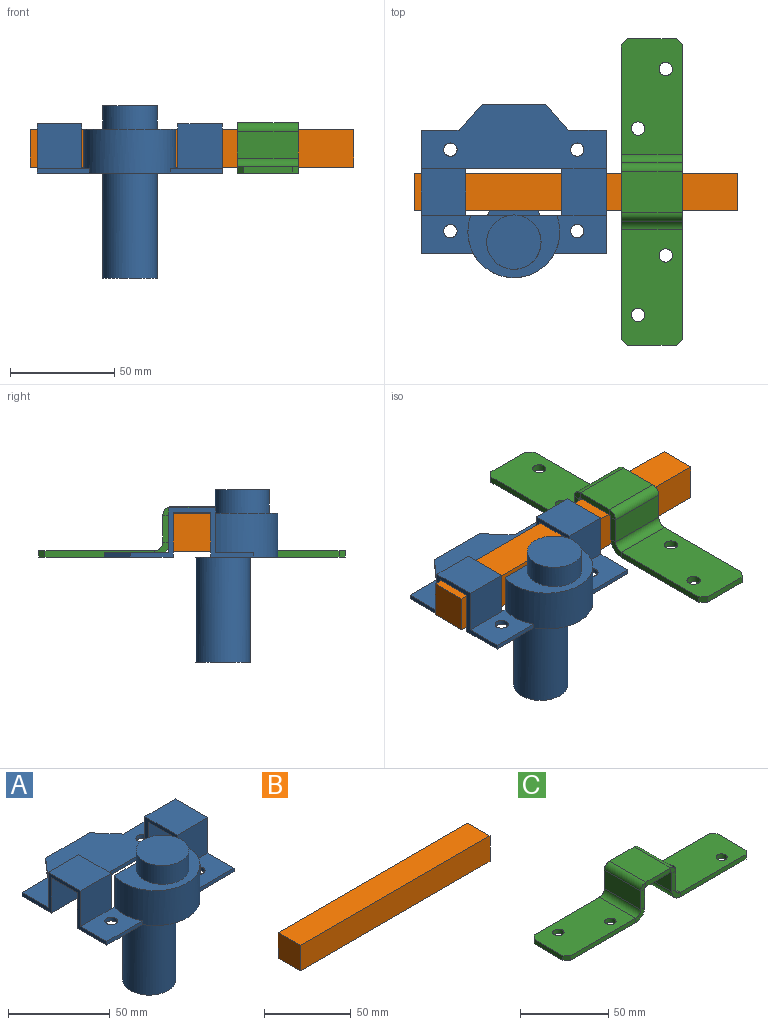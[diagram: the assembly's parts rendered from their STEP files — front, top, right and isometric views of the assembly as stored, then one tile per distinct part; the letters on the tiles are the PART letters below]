
ASSEMBLY  parts=3 mates=1
PART A: 42 faces, bbox 88.5x83x82.7 mm
  f0: plane 88.5x31.95mm, normal (0,0,-1), area 1605.4mm2, adj f1,f2,f3,f4,f13,f14,f15,f22
  f1: plane 59x23.5mm, normal (-1,0,0), area 223.5mm2, adj f0,f5,f6,f7,f8,f9,f10,f12
  f2: plane 59x23.5mm, normal (1,0,0), area 223.5mm2, adj f0,f7,f9,f15,f16,f19,f29,f30
  f3: plane 23.5x22.5mm, normal (-1,0,0), area 143.2mm2, adj f0,f7,f29,f30,f31,f33,f35,f39
  f4: plane 23.5x22.5mm, normal (1,0,0), area 143.2mm2, adj f0,f5,f6,f7,f8,f33,f35,f36
  f5: plane 21.3x21.25mm, normal (0,-1,0), area 452.6mm2, adj f1,f4,f8,f10
  f6: plane 21.3x21.25mm, normal (0,1,0), area 452.6mm2, adj f1,f4,f8,f9
  f7: plane 88.5x32.98mm, normal (0,0,-1), area 2164.3mm2, adj f1,f2,f3,f4,f11,f12,f16,f17
  f8: plane 22.5x21.25mm, normal (0,0,1), area 478.1mm2, adj f1,f4,f5,f6
  f9: plane 88.5x30.78mm, normal (0,0,1), area 2070.8mm2, adj f1,f2,f6,f11,f12,f16,f17,f18
  f10: plane 24.92x18.25mm, normal (0,0,1), area 386.6mm2, adj f1,f5,f13,f14,f23,f33
  f11: plane 12.53x11mm, normal (-0.75,0.66,0), area 36.7mm2, adj f7,f9,f12,f18
  f12: plane 18x2.2mm, normal (0,1,0), area 39.6mm2, adj f1,f7,f9,f11
  f13: plane 24.92x2.2mm, normal (0,-1,0), area 54.8mm2, adj f0,f1,f10,f14
  f14: cylinder r=22mm len=44mm, axis (0,0,-1), area 1701mm2, adj f0,f10,f13,f15,f19,f24,f33
  f15: plane 24.92x2.2mm, normal (0,-1,0), area 54.8mm2, adj f0,f2,f14,f19
  f16: plane 18x2.2mm, normal (0,1,0), area 39.6mm2, adj f2,f7,f9,f17
  f17: plane 12.53x11mm, normal (0.75,0.66,0), area 36.7mm2, adj f7,f9,f16,f18
  f18: plane 30.5x2.2mm, normal (0,1,0), area 67.1mm2, adj f7,f9,f11,f17
  f19: plane 24.92x18.25mm, normal (0,0,1), area 386.6mm2, adj f2,f14,f15,f22,f31,f33
  f20: cylinder r=3.2mm len=6.4mm, axis (0,0,-1), area 44.2mm2, adj f7,f9
  f21: cylinder r=3.2mm len=6.4mm, axis (0,0,-1), area 44.2mm2, adj f7,f9
  f22: cylinder r=3.2mm len=6.4mm, axis (0,0,-1), area 44.2mm2, adj f0,f19
  f23: cylinder r=3.2mm len=6.4mm, axis (0,0,-1), area 44.2mm2, adj f0,f10
  f24: plane 44x29.75mm, normal (0,0,1), area 564mm2, adj f14,f25,f33
  f25: cylinder r=13mm len=26mm, axis (0,0,-1), area 906.1mm2, adj f24,f26,f32,f33
  f26: plane 26x26mm, normal (0,0,1), area 530.9mm2, adj f25
  f27: cylinder r=13mm len=50.4mm, axis (0,0,1), area 4116.7mm2, adj f0,f28,f34
  f28: plane 26x26mm, normal (0,0,-1), area 530.9mm2, adj f27
  f29: plane 21.3x21.25mm, normal (0,1,0), area 452.6mm2, adj f2,f3,f9,f30
  f30: plane 22.5x21.25mm, normal (0,0,1), area 478.1mm2, adj f2,f3,f29,f31
  f31: plane 21.3x21.25mm, normal (0,-1,0), area 452.6mm2, adj f2,f3,f19,f30
  f32: plane 5.07x0.25mm, normal (0,0,-1), area 0.8mm2, adj f25,f33
  f33: plane 46x23.5mm, normal (0,1,0), area 888.1mm2, adj f0,f3,f4,f10,f14,f19,f24,f25
  f34: plane 25.04x9.5mm, normal (0,0,1), area 175.6mm2, adj f27,f33
  f35: plane 46x2.2mm, normal (0,-1,0), area 101.2mm2, adj f3,f4,f7,f9
  f36: plane 21.3x21.25mm, normal (0,1,0), area 452.6mm2, adj f0,f1,f4,f37
  f37: plane 21.25x18.1mm, normal (0,0,-1), area 384.6mm2, adj f1,f4,f36,f38
  f38: plane 21.3x21.25mm, normal (0,-1,0), area 452.6mm2, adj f1,f4,f7,f37
  f39: plane 21.3x21.25mm, normal (0,-1,0), area 452.6mm2, adj f2,f3,f7,f40
  f40: plane 21.25x18.1mm, normal (0,0,-1), area 384.6mm2, adj f2,f3,f39,f41
  f41: plane 21.3x21.25mm, normal (0,1,0), area 452.6mm2, adj f0,f2,f3,f40
PART B: 6 faces, bbox 155x18x18 mm
  f0: plane 155x18mm, normal (0,1,0), area 2790mm2, adj f1,f3,f4,f5
  f1: plane 155x18mm, normal (0,0,-1), area 2790mm2, adj f0,f2,f4,f5
  f2: plane 155x18mm, normal (0,-1,0), area 2790mm2, adj f1,f3,f4,f5
  f3: plane 155x18mm, normal (0,0,1), area 2790mm2, adj f0,f2,f4,f5
  f4: plane 18x18mm, normal (1,0,0), area 324mm2, adj f0,f1,f2,f3
  f5: plane 18x18mm, normal (-1,0,0), area 324mm2, adj f0,f1,f2,f3
PART C: 46 faces, bbox 146.8x29.2x24.1 mm
  f0: plane 12.9x3.1mm, normal (0,1,0), area 40mm2, adj f2,f3,f30,f43
  f1: plane 12.9x3.1mm, normal (0,-1,0), area 40mm2, adj f2,f3,f29,f42
  f2: plane 29.2x12.9mm, normal (1,0,0), area 376.7mm2, adj f0,f1,f32,f44
  f3: plane 29.2x12.9mm, normal (-1,0,0), area 376.7mm2, adj f0,f1,f31,f45
  f4: plane 19.75x3.1mm, normal (0,1,0), area 61.2mm2, adj f6,f7,f26,f30
  f5: plane 19.75x3.1mm, normal (0,-1,0), area 61.2mm2, adj f6,f7,f25,f29
  f6: plane 29.2x19.75mm, normal (0,0,-1), area 576.7mm2, adj f4,f5,f28,f32
  f7: plane 29.2x19.75mm, normal (0,0,1), area 576.7mm2, adj f4,f5,f27,f31
  f8: plane 12.9x3.1mm, normal (0,1,0), area 40mm2, adj f10,f11,f22,f26
  f9: plane 12.9x3.1mm, normal (0,-1,0), area 40mm2, adj f10,f11,f21,f25
  f10: plane 29.2x12.9mm, normal (-1,0,0), area 376.7mm2, adj f8,f9,f23,f28
  f11: plane 29.2x12.9mm, normal (1,0,0), area 376.7mm2, adj f8,f9,f24,f27
  f12: plane 23.2x3.1mm, normal (1,0,0), area 71.9mm2, adj f17,f18,f19,f20
  f13: plane 52.4x3.1mm, normal (0,-1,0), area 162.4mm2, adj f17,f18,f19,f21
  f14: cylinder r=3.2mm len=6.4mm, axis (0,0,-1), area 62.3mm2, adj f17,f18
  f15: cylinder r=3.2mm len=6.4mm, axis (0,0,-1), area 62.3mm2, adj f17,f18
  f16: plane 52.4x3.1mm, normal (0,1,0), area 162.4mm2, adj f17,f18,f20,f22
  f17: plane 55.4x29.2mm, normal (0,0,-1), area 1544.3mm2, adj f12,f13,f14,f15,f16,f19,f20,f23
  f18: plane 55.4x29.2mm, normal (0,0,1), area 1544.3mm2, adj f12,f13,f14,f15,f16,f19,f20,f24
  f19: plane 3.1x3mm, normal (0.71,-0.71,0), area 13.2mm2, adj f12,f13,f17,f18
  f20: plane 3.1x3mm, normal (0.71,0.71,0), area 13.2mm2, adj f12,f16,f17,f18
  f21: plane 7.1x7.1mm, normal (0,-1,0), area 27mm2, adj f9,f13,f23,f24
  f22: plane 7.1x7.1mm, normal (0,1,0), area 27mm2, adj f8,f16,f23,f24
  f23: cylinder r=7.1mm len=29.2mm, axis (0,-1,0), area 325.7mm2, adj f10,f17,f21,f22
  f24: cylinder r=4mm len=29.2mm, axis (0,-1,0), area 183.5mm2, adj f11,f18,f21,f22
  f25: plane 4.1x4.1mm, normal (0,-1,0), area 12.4mm2, adj f5,f9,f27,f28
  f26: plane 4.1x4.1mm, normal (0,1,0), area 12.4mm2, adj f4,f8,f27,f28
  f27: cylinder r=4.1mm len=29.2mm, axis (0,-1,0), area 188.1mm2, adj f7,f11,f25,f26
  f28: cylinder r=1mm len=29.2mm, axis (0,-1,0), area 45.9mm2, adj f6,f10,f25,f26
  f29: plane 4.1x4.1mm, normal (0,-1,0), area 12.4mm2, adj f1,f5,f31,f32
  f30: plane 4.1x4.1mm, normal (0,1,0), area 12.4mm2, adj f0,f4,f31,f32
  f31: cylinder r=4.1mm len=29.2mm, axis (0,-1,0), area 188.1mm2, adj f3,f7,f29,f30
  f32: cylinder r=1mm len=29.2mm, axis (0,-1,0), area 45.9mm2, adj f2,f6,f29,f30
  f33: plane 23.2x3.1mm, normal (-1,0,0), area 71.9mm2, adj f38,f39,f40,f41
  f34: plane 52.4x3.1mm, normal (0,1,0), area 162.4mm2, adj f38,f39,f41,f43
  f35: cylinder r=3.2mm len=6.4mm, axis (0,0,-1), area 62.3mm2, adj f38,f39
  f36: cylinder r=3.2mm len=6.4mm, axis (0,0,-1), area 62.3mm2, adj f38,f39
  f37: plane 52.4x3.1mm, normal (0,-1,0), area 162.4mm2, adj f38,f39,f40,f42
  f38: plane 55.4x29.2mm, normal (0,0,-1), area 1544.3mm2, adj f33,f34,f35,f36,f37,f40,f41,f44
  f39: plane 55.4x29.2mm, normal (0,0,1), area 1544.3mm2, adj f33,f34,f35,f36,f37,f40,f41,f45
  f40: plane 3.1x3mm, normal (-0.71,-0.71,0), area 13.2mm2, adj f33,f37,f38,f39
  f41: plane 3.1x3mm, normal (-0.71,0.71,0), area 13.2mm2, adj f33,f34,f38,f39
  f42: plane 7.1x7.1mm, normal (0,-1,0), area 27mm2, adj f1,f37,f44,f45
  f43: plane 7.1x7.1mm, normal (0,1,0), area 27mm2, adj f0,f34,f44,f45
  f44: cylinder r=7.1mm len=29.2mm, axis (0,-1,0), area 325.7mm2, adj f2,f38,f42,f43
  f45: cylinder r=4mm len=29.2mm, axis (0,-1,0), area 183.5mm2, adj f3,f39,f42,f43
PLACE A t=(33.51,8.24,49.33)mm
PLACE B t=(30.01,8.24,49.1)mm
PLACE C rot(axis=(0,0,1),90deg) t=(99.61,8.28,49.33)mm
MATE slider B.f4 <-> A.f2  axis (1,0,0) through (140.76,8.24,61.15)mm
